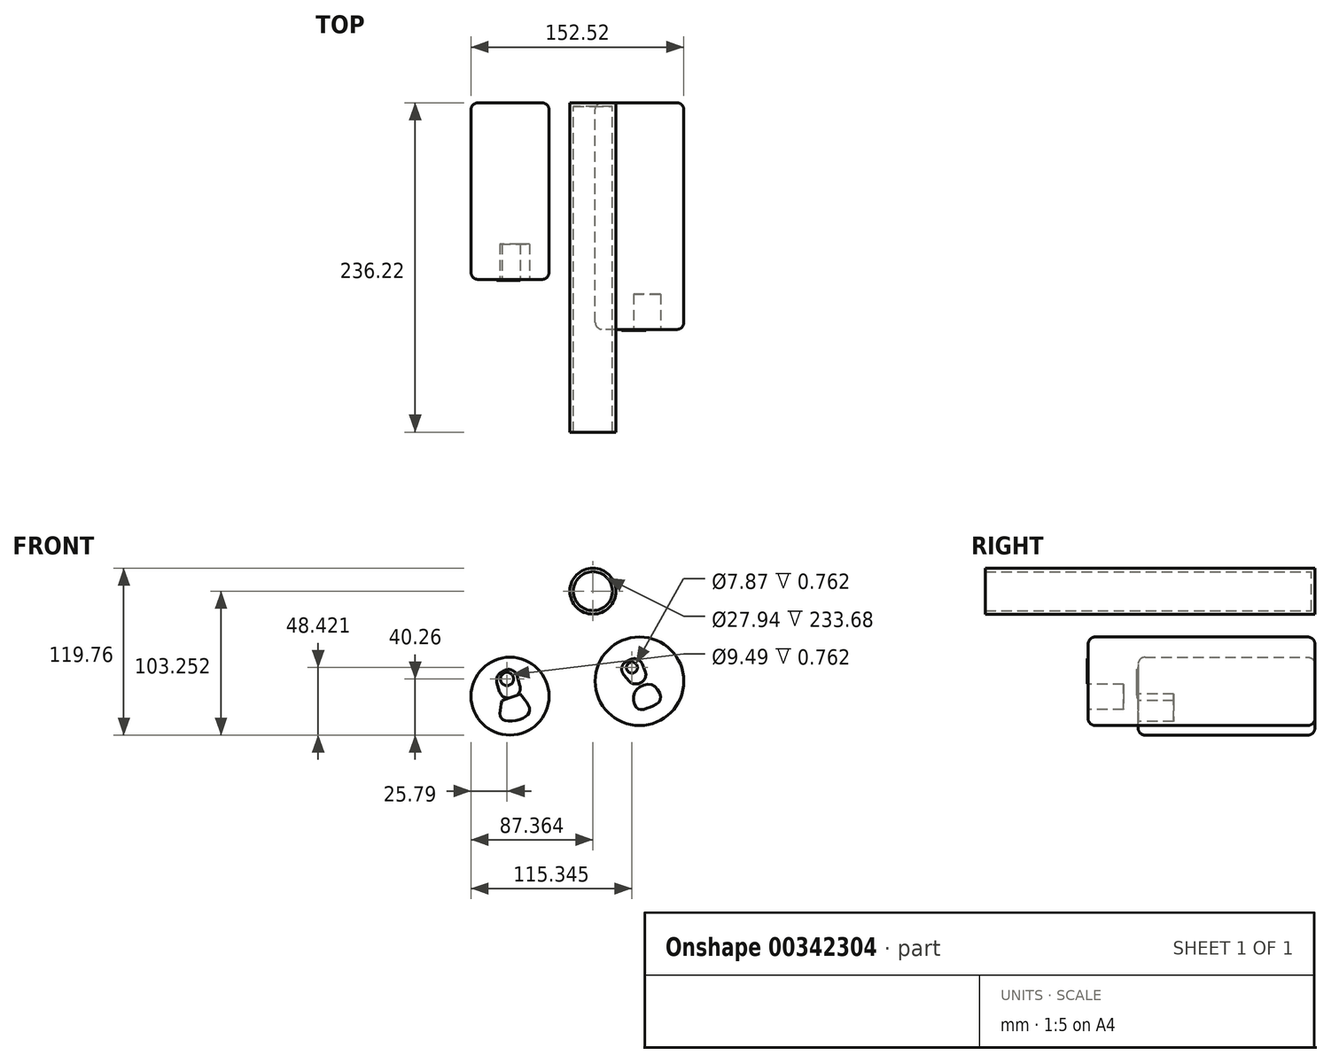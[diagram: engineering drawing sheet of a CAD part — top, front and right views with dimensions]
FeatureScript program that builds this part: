
annotation { "Feature Type Name" : "Feature", "Feature Type Description" : "" }
export const myFeature = defineFeature(function(context is Context, id is Id, definition is map)
    precondition{}
    {
        {
            var Q0;
            Q0=qCreatedBy(makeId("Front.planeOp"),FACE);
            var sketch = newSketch(context, id + "F0", { "sketchPlane" : qUnion([Q0])});
            skCircle(sketch, "E0", {"center": v(18.61, 44.48) * mm, "radius": 16.51 * mm});
            skCircle(sketch, "E1", {"center": v(-40.81, -30.83) * mm, "radius": 27.94 * mm});
            skCircle(sketch, "E2", {"center": v(52.02, -20.15) * mm, "radius": 31.75 * mm});
            skSolve(sketch);
        }
        {
            var Q0;
            Q0=makeQuery(id+"F0.imprint","IMPRINT",FACE,{"disambiguationData":[TD([[makeQuery(id+"F0.imprint","IMPRINT",EDGE,{"derivedFrom":sQuery(id+"F0.wireOp",EDGE,"E1")}),1.0]])]});
            extrude(context, id + "F1", {"entities" : qUnion([Q0]), "depth" : 126.75 * mm});
        }
        {
            var Q0;
            Q0=makeQuery(id+"F0.imprint","IMPRINT",FACE,{"disambiguationData":[TD([[makeQuery(id+"F0.imprint","IMPRINT",EDGE,{"derivedFrom":sQuery(id+"F0.wireOp",EDGE,"E2")}),1.0]])]});
            extrude(context, id + "F2", {"entities" : qUnion([Q0]), "depth" : 162.56 * mm});
        }
        {
            var Q0;
            Q0=makeQuery(id+"F0.imprint","IMPRINT",FACE,{"disambiguationData":[TD([[makeQuery(id+"F0.imprint","IMPRINT",EDGE,{"derivedFrom":sQuery(id+"F0.wireOp",EDGE,"E0")}),1.0]])]});
            extrude(context, id + "F3", {"entities" : qUnion([Q0]), "depth" : 236.22 * mm});
        }
        {
            var Q0;
            Q0=makeQuery(id+"F1.opExtrude","CAP_EDGE",EDGE,{"disambiguationData":[OSD([sQuery(id+"F0.wireOp",EDGE,"E1")])],"isStart":false});
            fillet(context, id + "F4", {"entities" : qUnion([Q0]), "radius" : 5.08 * mm, "tangentPropagation" : true, "allowEdgeOverflow" : false});
        }
        {
            var Q0;
            Q0=makeQuery(id+"F2.opExtrude","CAP_EDGE",EDGE,{"disambiguationData":[OSD([sQuery(id+"F0.wireOp",EDGE,"E2")])],"isStart":false});
            fillet(context, id + "F5", {"entities" : qUnion([Q0]), "radius" : 5.08 * mm, "tangentPropagation" : true, "allowEdgeOverflow" : false});
        }
        {
            var Q0;
            Q0=makeQuery(id+"F3.opExtrude","CAP_FACE",FACE,{"disambiguationData":[OSD([sQuery(id+"F0.wireOp",EDGE,"E0")])],"isStart":false});
            shell(context, id + "F6", {"entities" : qUnion([Q0]), "thickness" : 2.54 * mm});
        }
        {
            var Q0;
            Q0=makeQuery(id+"F1.opExtrude","CAP_FACE",FACE,{"disambiguationData":[OSD([sQuery(id+"F0.wireOp",EDGE,"E1")])],"isStart":false});
            var sketch = newSketch(context, id + "F7", { "sketchPlane" : qUnion([Q0])});
            skFitSpline(sketch, "E3", {"points": [v(-46.53, -33.95) * mm, v(-45.69, -47.84) * mm, v(-27.49, -43.6) * mm, v(-33.52, -29.24) * mm], "startDerivative": vector(-13.68, -56.67) * mm, "endDerivative": vector(-39.3, 47.94) * mm});
            skLineSegment(sketch, "E4", {"start": v(-33.52, -29.24) * mm, "end": v(-46.53, -33.95) * mm});
            skSolve(sketch);
        }
        {
            var Q0;
            Q0=makeQuery(id+"F7.imprint","IMPRINT",FACE,{"disambiguationData":[TD([[makeQuery(id+"F7.imprint","IMPRINT",EDGE,{"derivedFrom":sQuery(id+"F7.wireOp",EDGE,"E3")}),1.0]])]});
            extrude(context, id + "F8", {"entities" : qUnion([Q0]), "operationType" : NewBodyOperationType.REMOVE, "oppositeDirection" : true, "depth" : 25.4 * mm});
        }
        {
            var Q0;
            Q0=makeQuery(id+"F2.opExtrude","CAP_FACE",FACE,{"disambiguationData":[OSD([sQuery(id+"F0.wireOp",EDGE,"E2")])],"isStart":false});
            var sketch = newSketch(context, id + "F9", { "sketchPlane" : qUnion([Q0])});
            skFitSpline(sketch, "E5", {"points": [v(48.47, -28.45) * mm, v(50.73, -39.8) * mm, v(58.66, -39.03) * mm, v(66.82, -33.4) * mm, v(61.14, -22.86) * mm, v(48.47, -28.45) * mm]});
            skSolve(sketch);
        }
        {
            var Q0;
            Q0=makeQuery(id+"F9.imprint","IMPRINT",FACE,{"disambiguationData":[TD([[makeQuery(id+"F9.imprint","IMPRINT",EDGE,{"derivedFrom":sQuery(id+"F9.wireOp",EDGE,"E5")}),1.0]])]});
            extrude(context, id + "F10", {"entities" : qUnion([Q0]), "operationType" : NewBodyOperationType.REMOVE, "oppositeDirection" : true, "depth" : 25.4 * mm});
        }
        {
            var Q0;
            Q0=makeQuery(id+"F1.opExtrude","CAP_EDGE",EDGE,{"disambiguationData":[OSD([sQuery(id+"F0.wireOp",EDGE,"E1")])],"isStart":true});
            var Q1;
            Q1=makeQuery(id+"F2.opExtrude","CAP_EDGE",EDGE,{"disambiguationData":[OSD([sQuery(id+"F0.wireOp",EDGE,"E2")])],"isStart":true});
            fillet(context, id + "F11", {"entities" : qUnion([Q0, Q1]), "radius" : 5.08 * mm, "tangentPropagation" : true, "allowEdgeOverflow" : false});
        }
        {
            var Q0;
            Q0=makeQuery(id+"F7.imprint","IMPRINT",FACE,{"disambiguationData":[TD([[makeQuery(id+"F7.imprint","IMPRINT",EDGE,{"derivedFrom":sQuery(id+"F7.wireOp",EDGE,"E3")}),-1.0]])]});
            var sketch = newSketch(context, id + "F12", { "sketchPlane" : qUnion([Q0])});
            skLineSegment(sketch, "E6", {"start": v(-50.2, -20.96) * mm, "end": v(-48.3, -27.57) * mm});
            skLineSegment(sketch, "E7", {"start": v(-40.45, -31.92) * mm, "end": v(-38.07, -31.23) * mm});
            skLineSegment(sketch, "E8", {"start": v(-33.73, -23.37) * mm, "end": v(-35.78, -16.24) * mm});
            skLineSegment(sketch, "E9", {"start": v(-44.91, -12.42) * mm, "end": v(-47.14, -13.63) * mm});
            skPoint(sketch, "E10.visualSharp", {"position": v(-51.62, -16.06) * mm});
            skArc(sketch, "E10.filletArc", {"start": v(-47.14, -13.63) * mm, "mid": v(-49.96, -16.75) * mm, "end": v(-50.2, -20.96) * mm});
            skPoint(sketch, "E11.visualSharp", {"position": v(-37.96, -8.64) * mm});
            skArc(sketch, "E11.filletArc", {"start": v(-35.78, -16.24) * mm, "mid": v(-39.43, -12.14) * mm, "end": v(-44.91, -12.42) * mm});
            skPoint(sketch, "E12.visualSharp", {"position": v(-31.97, -29.48) * mm});
            skArc(sketch, "E12.filletArc", {"start": v(-38.07, -31.23) * mm, "mid": v(-34.27, -28.2) * mm, "end": v(-33.73, -23.37) * mm});
            skPoint(sketch, "E13.visualSharp", {"position": v(-46.55, -33.67) * mm});
            skArc(sketch, "E13.filletArc", {"start": v(-48.3, -27.57) * mm, "mid": v(-45.28, -31.37) * mm, "end": v(-40.45, -31.92) * mm});
            skSolve(sketch);
        }
        {
            var Q0;
            {var subQ6=sQuery(id+"F12.wireOp",EDGE,"E6");Q0=makeQuery(id+"F12.imprint","IMPRINT",FACE,{"disambiguationData":[TD([[makeQuery(id+"F12.imprint","IMPRINT",EDGE,{"derivedFrom":subQ6}),1.0]])]});}
            extrude(context, id + "F13", {"entities" : qUnion([Q0]), "operationType" : NewBodyOperationType.ADD, "depth" : 0.76 * mm});
        }
        {
            var Q0;
            Q0=makeQuery(id+"F13.opExtrude","CAP_FACE",FACE,{"disambiguationData":[OSD([sQuery(id+"F7.wireOp",EDGE,"E4"),sQuery(id+"F12.wireOp",EDGE,"E6"),sQuery(id+"F12.wireOp",EDGE,"E8"),sQuery(id+"F12.wireOp",EDGE,"E9"),sQuery(id+"F12.wireOp",EDGE,"E10.filletArc"),sQuery(id+"F12.wireOp",EDGE,"E11.filletArc"),sQuery(id+"F12.wireOp",EDGE,"E12.filletArc"),sQuery(id+"F12.wireOp",EDGE,"E13.filletArc")])],"isStart":false});
            var sketch = newSketch(context, id + "F14", { "sketchPlane" : qUnion([Q0])});
            skCircle(sketch, "E14", {"center": v(-42.96, -18.51) * mm, "radius": 4.74 * mm});
            skSolve(sketch);
        }
        {
            var Q0;
            Q0=makeQuery(id+"F14.imprint","IMPRINT",FACE,{"disambiguationData":[TD([[makeQuery(id+"F14.imprint","IMPRINT",EDGE,{"derivedFrom":sQuery(id+"F14.wireOp",EDGE,"E14")}),1.0]])]});
            var Q1;
            Q1=makeQuery(id+"F1.opExtrude","CAP_FACE",FACE,{"disambiguationData":[OSD([sQuery(id+"F0.wireOp",EDGE,"E1")])],"isStart":false});
            extrude(context, id + "F15", {"entities" : qUnion([Q0]), "operationType" : NewBodyOperationType.REMOVE, "endBound" : BoundingType.UP_TO_SURFACE, "oppositeDirection" : true, "endBoundEntityFace" : qUnion([Q1]), "depth" : 25.4 * mm});
        }
        {
            var Q0;
            Q0=makeQuery(id+"F2.opExtrude","CAP_FACE",FACE,{"disambiguationData":[OSD([sQuery(id+"F0.wireOp",EDGE,"E2")])],"isStart":false});
            var sketch = newSketch(context, id + "F16", { "sketchPlane" : qUnion([Q0])});
            skLineSegment(sketch, "E15", {"start": v(40.82, -15.66) * mm, "end": v(44.57, -19.95) * mm});
            skLineSegment(sketch, "E16", {"start": v(51.75, -21.65) * mm, "end": v(52.58, -21.31) * mm});
            skLineSegment(sketch, "E17", {"start": v(56.06, -13.03) * mm, "end": v(53.99, -7.94) * mm});
            skLineSegment(sketch, "E18", {"start": v(45.47, -4.56) * mm, "end": v(42.96, -5.7) * mm});
            skPoint(sketch, "E19.visualSharp", {"position": v(35.22, -9.25) * mm});
            skArc(sketch, "E19.filletArc", {"start": v(42.96, -5.7) * mm, "mid": v(39.4, -10.14) * mm, "end": v(40.82, -15.66) * mm});
            skPoint(sketch, "E20.visualSharp", {"position": v(51.49, -1.81) * mm});
            skArc(sketch, "E20.filletArc", {"start": v(53.99, -7.94) * mm, "mid": v(50.45, -4.43) * mm, "end": v(45.47, -4.56) * mm});
            skPoint(sketch, "E21.visualSharp", {"position": v(58.46, -18.91) * mm});
            skArc(sketch, "E21.filletArc", {"start": v(52.58, -21.31) * mm, "mid": v(56.04, -17.9) * mm, "end": v(56.06, -13.03) * mm});
            skPoint(sketch, "E22.visualSharp", {"position": v(47.55, -23.37) * mm});
            skArc(sketch, "E22.filletArc", {"start": v(44.57, -19.95) * mm, "mid": v(47.89, -21.95) * mm, "end": v(51.75, -21.65) * mm});
            skSolve(sketch);
        }
        {
            var Q0;
            Q0=makeQuery(id+"F16.imprint","IMPRINT",FACE,{"disambiguationData":[TD([[makeQuery(id+"F16.imprint","IMPRINT",EDGE,{"derivedFrom":sQuery(id+"F16.wireOp",EDGE,"E15")}),1.0]])]});
            extrude(context, id + "F17", {"entities" : qUnion([Q0]), "operationType" : NewBodyOperationType.ADD, "depth" : 0.76 * mm});
        }
        {
            var Q0;
            Q0=makeQuery(id+"F17.opExtrude","CAP_FACE",FACE,{"disambiguationData":[OSD([sQuery(id+"F16.wireOp",EDGE,"E15"),sQuery(id+"F16.wireOp",EDGE,"E16"),sQuery(id+"F16.wireOp",EDGE,"E17"),sQuery(id+"F16.wireOp",EDGE,"E18"),sQuery(id+"F16.wireOp",EDGE,"E19.filletArc"),sQuery(id+"F16.wireOp",EDGE,"E20.filletArc"),sQuery(id+"F16.wireOp",EDGE,"E21.filletArc"),sQuery(id+"F16.wireOp",EDGE,"E22.filletArc")])],"isStart":false});
            var sketch = newSketch(context, id + "F18", { "sketchPlane" : qUnion([Q0])});
            skCircle(sketch, "E23", {"center": v(46.6, -10.35) * mm, "radius": 3.94 * mm});
            skSolve(sketch);
        }
        {
            var Q0;
            Q0=makeQuery(id+"F18.imprint","IMPRINT",FACE,{"disambiguationData":[TD([[makeQuery(id+"F18.imprint","IMPRINT",EDGE,{"derivedFrom":sQuery(id+"F18.wireOp",EDGE,"E23")}),1.0]])]});
            var Q1;
            Q1=makeQuery(id+"F2.opExtrude","CAP_FACE",FACE,{"disambiguationData":[OSD([sQuery(id+"F0.wireOp",EDGE,"E2")])],"isStart":false});
            extrude(context, id + "F19", {"entities" : qUnion([Q0]), "operationType" : NewBodyOperationType.REMOVE, "endBound" : BoundingType.UP_TO_SURFACE, "oppositeDirection" : true, "endBoundEntityFace" : qUnion([Q1]), "depth" : 25.4 * mm});
        }
    });
